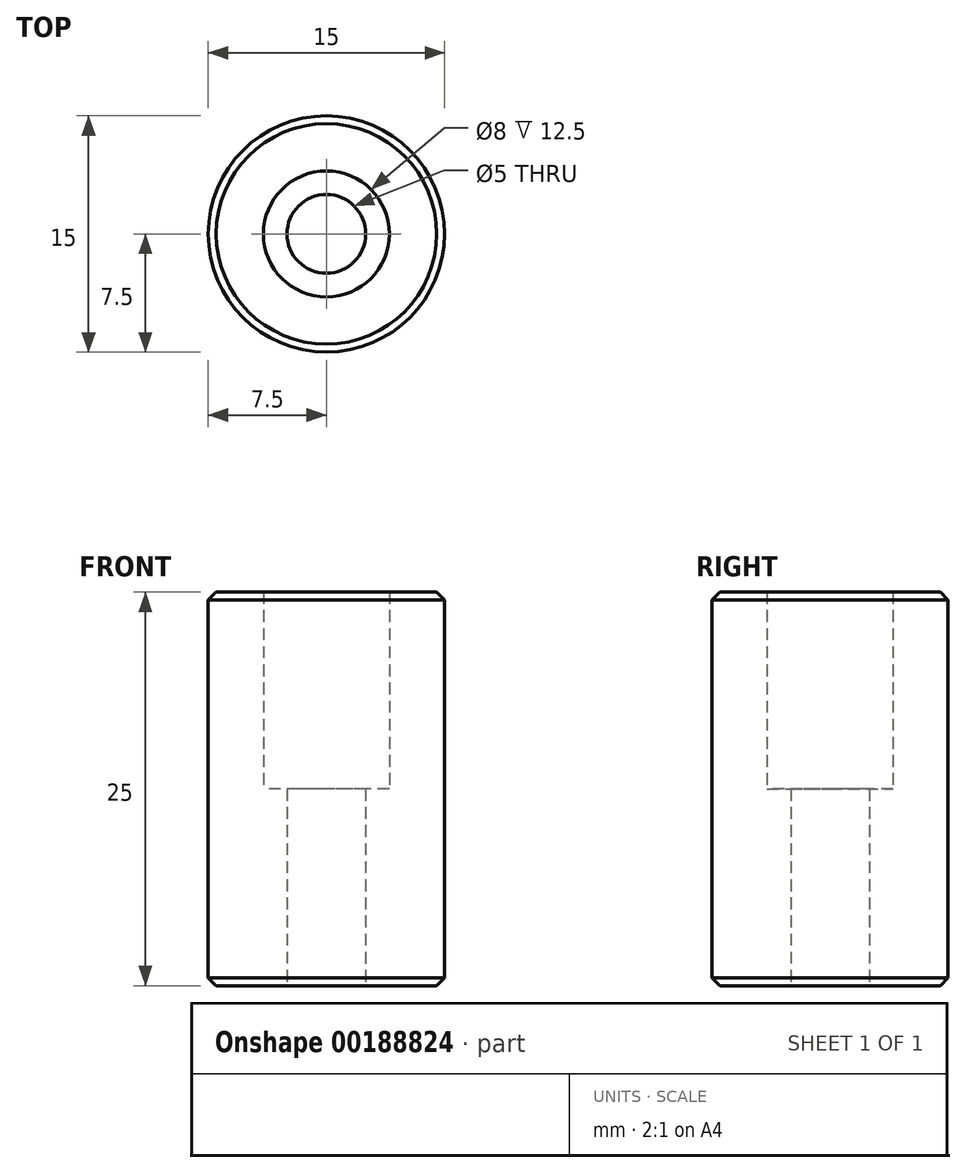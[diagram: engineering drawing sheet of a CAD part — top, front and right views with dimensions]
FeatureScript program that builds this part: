
annotation { "Feature Type Name" : "Feature", "Feature Type Description" : "" }
export const myFeature = defineFeature(function(context is Context, id is Id, definition is map)
    precondition{}
    {
        {
            var Q0;
            Q0=qCreatedBy(makeId("Top.planeOp"),FACE);
            var sketch = newSketch(context, id + "F0", { "sketchPlane" : qUnion([Q0])});
            skCircle(sketch, "E0", {"center": v(0, 0) * mm, "radius": 7.5 * mm});
            skCircle(sketch, "E1", {"center": v(0, 0) * mm, "radius": 4 * mm});
            skCircle(sketch, "E2", {"center": v(0, 0) * mm, "radius": 2.5 * mm});
            skSolve(sketch);
        }
        {
            var Q0;
            Q0=makeQuery(id+"F0.imprint","IMPRINT",FACE,{"disambiguationData":[TD([[makeQuery(id+"F0.imprint","IMPRINT",EDGE,{"derivedFrom":sQuery(id+"F0.wireOp",EDGE,"E0")}),1.0]])]});
            extrude(context, id + "F1", {"entities" : qUnion([Q0]), "depth" : 25 * mm});
        }
        {
            var Q0;
            Q0=makeQuery(id+"F0.imprint","IMPRINT",FACE,{"disambiguationData":[TD([[makeQuery(id+"F0.imprint","IMPRINT",EDGE,{"derivedFrom":sQuery(id+"F0.wireOp",EDGE,"E2")}),1.0]])]});
            var Q1;
            Q1=makeQuery(id+"F0.imprint","IMPRINT",FACE,{"disambiguationData":[TD([[makeQuery(id+"F0.imprint","IMPRINT",EDGE,{"derivedFrom":sQuery(id+"F0.wireOp",EDGE,"E1")}),1.0]])]});
            extrude(context, id + "F2", {"entities" : qUnion([Q0, Q1]), "operationType" : NewBodyOperationType.ADD, "depth" : 12.5 * mm});
        }
        {
            var Q0;
            Q0=makeQuery(id+"F0.imprint","IMPRINT",FACE,{"disambiguationData":[TD([[makeQuery(id+"F0.imprint","IMPRINT",EDGE,{"derivedFrom":sQuery(id+"F0.wireOp",EDGE,"E2")}),1.0]])]});
            extrude(context, id + "F3", {"entities" : qUnion([Q0]), "operationType" : NewBodyOperationType.REMOVE, "depth" : 12.5 * mm});
        }
        {
            var Q0;
            Q0=makeQuery(id+"F1.opExtrude","CAP_EDGE",EDGE,{"disambiguationData":[OSD([sQuery(id+"F0.wireOp",EDGE,"E0")])],"isStart":false});
            var Q1;
            Q1=makeQuery(id+"F1.opExtrude","CAP_EDGE",EDGE,{"disambiguationData":[OSD([sQuery(id+"F0.wireOp",EDGE,"E0")])],"isStart":true});
            chamfer(context, id + "F4", {"entities" : qUnion([Q0, Q1]), "width" : .5 * mm, "tangentPropagation" : true});
        }
    });
